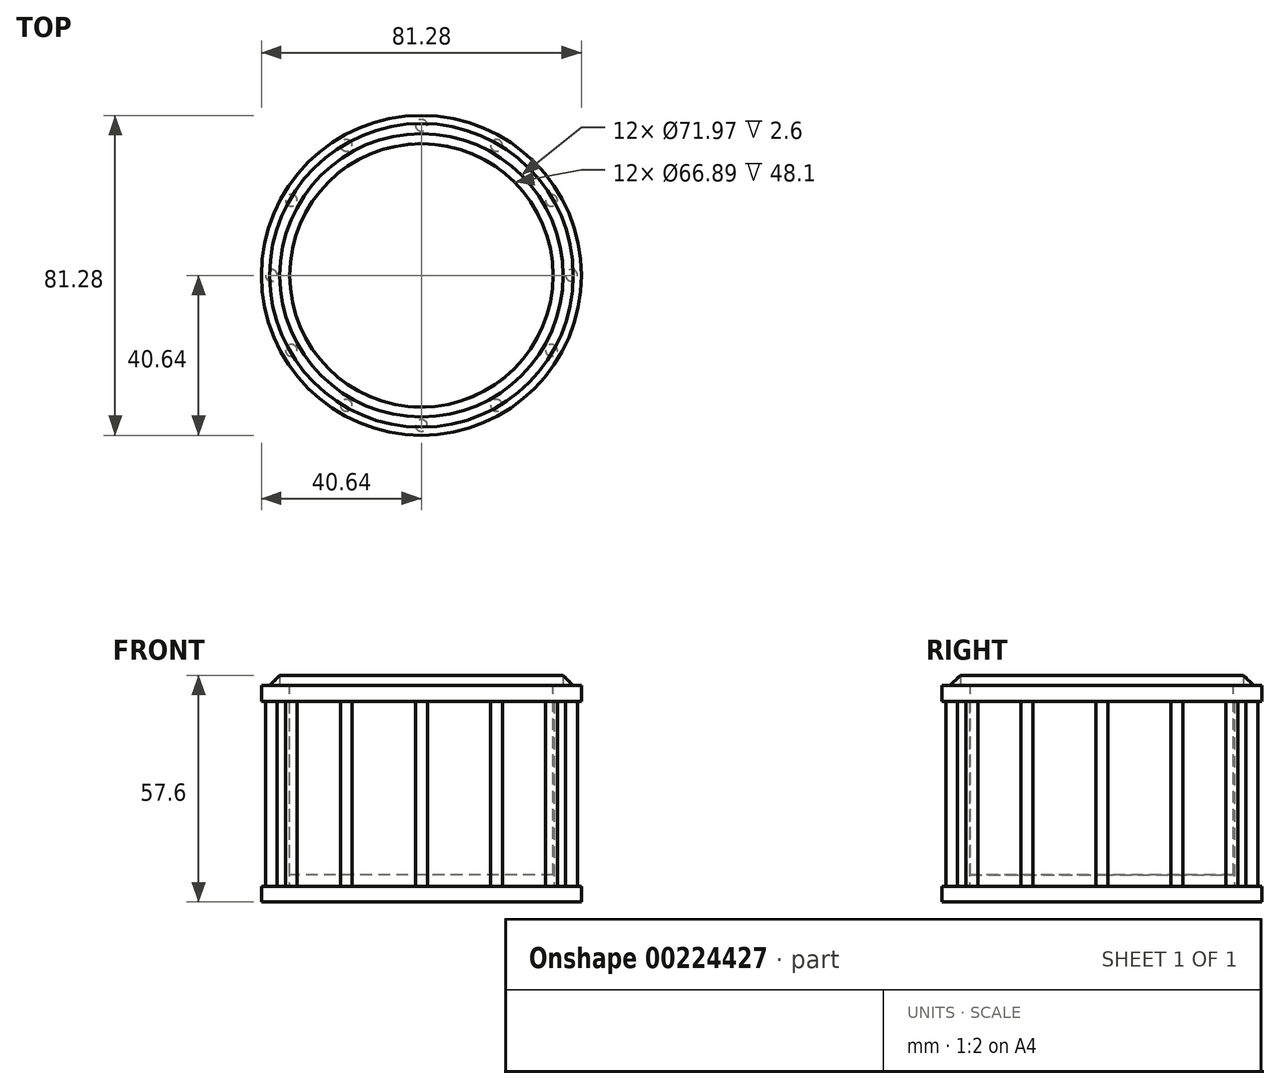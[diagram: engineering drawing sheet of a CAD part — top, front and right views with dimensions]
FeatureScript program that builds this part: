
annotation { "Feature Type Name" : "Feature", "Feature Type Description" : "" }
export const myFeature = defineFeature(function(context is Context, id is Id, definition is map)
    precondition{}
    {
        {
            var Q0;
            Q0=qCreatedBy(makeId("Top.planeOp"),FACE);
            var sketch = newSketch(context, id + "F0", { "sketchPlane" : qUnion([Q0])});
            skCircle(sketch, "E0", {"center": v(0, 0) * mm, "radius": 40.64 * mm});
            skSolve(sketch);
        }
        {
            var Q0;
            Q0=makeQuery(id+"F0.imprint","IMPRINT",FACE,{"disambiguationData":[TD([[makeQuery(id+"F0.imprint","IMPRINT",EDGE,{"derivedFrom":sQuery(id+"F0.wireOp",EDGE,"E0")}),1.0]])]});
            extrude(context, id + "F1", {"entities" : qUnion([Q0]), "depth" : 4 * mm});
        }
        {
            var Q0;
            Q0=makeQuery(id+"F1.opExtrude","CAP_FACE",FACE,{"disambiguationData":[OSD([sQuery(id+"F0.wireOp",EDGE,"E0")])],"isStart":false});
            var sketch = newSketch(context, id + "F2", { "sketchPlane" : qUnion([Q0])});
            skCircle(sketch, "E1", {"center": v(0, 0) * mm, "radius": 33.62 * mm});
            skSolve(sketch);
        }
        {
            var Q0;
            Q0=makeQuery(id+"F2.imprint","IMPRINT",FACE,{"disambiguationData":[TD([[makeQuery(id+"F2.imprint","IMPRINT",EDGE,{"derivedFrom":sQuery(id+"F2.wireOp",EDGE,"E1")}),1.0]])]});
            extrude(context, id + "F3", {"entities" : qUnion([Q0]), "operationType" : NewBodyOperationType.ADD, "depth" : 47 * mm});
        }
        {
            var Q0;
            Q0=makeQuery(id+"F3.opExtrude","CAP_FACE",FACE,{"disambiguationData":[OSD([sQuery(id+"F2.wireOp",EDGE,"E1")])],"isStart":false});
            var sketch = newSketch(context, id + "F4", { "sketchPlane" : qUnion([Q0])});
            skCircle(sketch, "E2", {"center": v(0, 0) * mm, "radius": 40.64 * mm});
            skSolve(sketch);
        }
        {
            var Q0;
            Q0=makeQuery(id+"F4.imprint","IMPRINT",FACE,{"disambiguationData":[TD([[makeQuery(id+"F4.imprint","IMPRINT",EDGE,{"derivedFrom":makeQuery(id+"F3.opExtrude","CAP_EDGE",EDGE,{"disambiguationData":[OSD([sQuery(id+"F2.wireOp",EDGE,"E1")])],"isStart":false})}),1.0]])]});
            var Q1;
            Q1=makeQuery(id+"F4.imprint","IMPRINT",FACE,{"disambiguationData":[TD([[makeQuery(id+"F4.imprint","IMPRINT",EDGE,{"derivedFrom":sQuery(id+"F4.wireOp",EDGE,"E2")}),1.0]])]});
            extrude(context, id + "F5", {"entities" : qUnion([Q0, Q1]), "operationType" : NewBodyOperationType.ADD, "depth" : 4 * mm});
        }
        {
            var Q0;
            Q0=qCreatedBy(makeId("Right.planeOp"),FACE);
            var sketch = newSketch(context, id + "F6", { "sketchPlane" : qUnion([Q0])});
            skLineSegment(sketch, "E3", {"start": v(-40.64, 55) * mm, "end": v(-38.57, 55) * mm, "construction": true});
            skLineSegment(sketch, "E4", {"start": v(-38.57, 55) * mm, "end": v(-35.98, 57.6) * mm});
            skLineSegment(sketch, "E5", {"start": v(-35.98, 57.6) * mm, "end": v(-35.98, 55) * mm});
            skLineSegment(sketch, "E6", {"start": v(-35.98, 55) * mm, "end": v(-38.57, 55) * mm});
            skLineSegment(sketch, "E7", {"start": v(0, 54.91) * mm, "end": v(0, 62.37) * mm, "construction": true});
            skSolve(sketch);
        }
        {
            var Q0;
            Q0=makeQuery(id+"F6.imprint","IMPRINT",FACE,{"disambiguationData":[TD([[makeQuery(id+"F6.imprint","IMPRINT",EDGE,{"derivedFrom":sQuery(id+"F6.wireOp",EDGE,"E4")}),-1.0]])]});
            var Q1;
            Q1=sQuery(id+"F6.wireOp",EDGE,"E7");
            revolve(context, id + "F7", {"operationType" : NewBodyOperationType.ADD, "entities" : qUnion([Q0]), "axis" : qUnion([Q1]), "revolveType" : RevolveType.FULL});
        }
        {
            var Q0;
            Q0=makeQuery(id+"F0.imprint","IMPRINT",FACE,{"disambiguationData":[TD([[makeQuery(id+"F0.imprint","IMPRINT",EDGE,{"derivedFrom":sQuery(id+"F0.wireOp",EDGE,"E0")}),1.0]])]});
            var sketch = newSketch(context, id + "F8", { "sketchPlane" : qUnion([Q0])});
            skCircle(sketch, "E8", {"center": v(0, -38.14) * mm, "radius": 1.5 * mm});
            skSolve(sketch);
        }
        {
            var Q0;
            Q0=makeQuery(id+"F8.imprint","IMPRINT",FACE,{"disambiguationData":[TD([[makeQuery(id+"F8.imprint","IMPRINT",EDGE,{"derivedFrom":sQuery(id+"F8.wireOp",EDGE,"E8")}),1.0]])]});
            extrude(context, id + "F9", {"entities" : qUnion([Q0]), "operationType" : NewBodyOperationType.ADD, "depth" : 55 * mm});
        }
        {
            var Q0;
            Q0=qCreatedBy(makeId("Front.planeOp"),FACE);
            var sketch = newSketch(context, id + "F10", { "sketchPlane" : qUnion([Q0])});
            skLineSegment(sketch, "E9", {"start": v(0, -17.8) * mm, "end": v(0, 61.94) * mm, "construction": true});
            skSolve(sketch);
        }
        {
            var Q0;
            Q0=makeQuery(id+"F1.opExtrude","SWEPT_BODY",BODY,{"disambiguationData":[OSD([sQuery(id+"F0.wireOp",EDGE,"E0")])]});
            var Q1;
            Q1=sQuery(id+"F10.wireOp",EDGE,"E9");
            circularPattern(context, id + "F11", {"entities" : qUnion([Q0]), "axis" : qUnion([Q1]), "angle" : 360 * degree, "instanceCount" : 12, "equalSpace" : true});
        }
        {
            var Q0;
            Q0=makeQuery(id+"F7.boolean.opBoolean","SPLIT",FACE,{"disambiguationData":[TD([makeQuery(id+"F7.opRevolve","SWEPT_FACE",FACE,{"disambiguationData":[OSD([sQuery(id+"F6.wireOp",EDGE,"E5")])]})])],"derivedFrom":makeQuery(id+"F5.opExtrude","CAP_FACE",FACE,{"disambiguationData":[OSD([sQuery(id+"F4.wireOp",EDGE,"E2")])],"isStart":false})});
            var sketch = newSketch(context, id + "F12", { "sketchPlane" : qUnion([Q0])});
            skCircle(sketch, "E10", {"center": v(0, 0) * mm, "radius": 33.45 * mm});
            skSolve(sketch);
        }
        {
            var Q0;
            Q0=makeQuery(id+"F12.imprint","IMPRINT",FACE,{"disambiguationData":[TD([[makeQuery(id+"F12.imprint","IMPRINT",EDGE,{"derivedFrom":sQuery(id+"F12.wireOp",EDGE,"E10")}),1.0]])]});
            extrude(context, id + "F13", {"entities" : qUnion([Q0]), "operationType" : NewBodyOperationType.REMOVE, "endBound" : BoundingType.SYMMETRIC, "oppositeDirection" : true, "depth" : 96.2 * mm});
        }
    });
